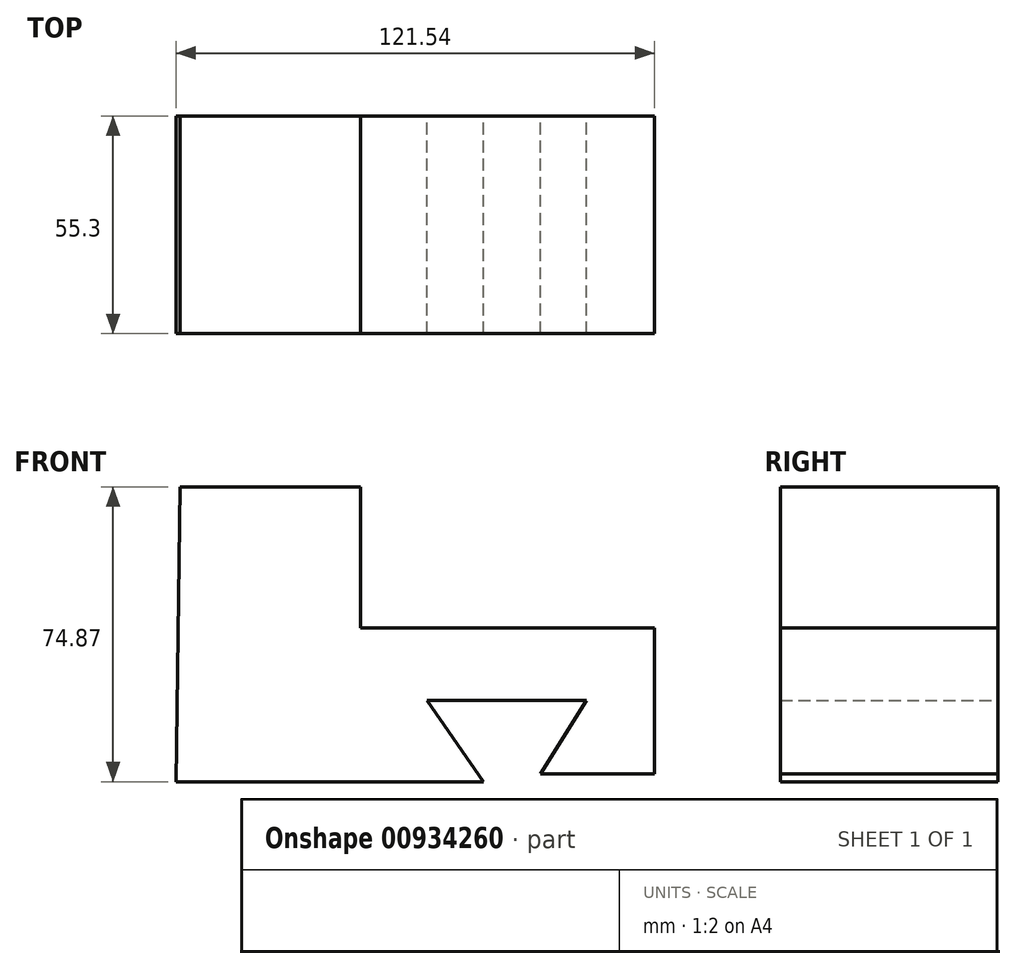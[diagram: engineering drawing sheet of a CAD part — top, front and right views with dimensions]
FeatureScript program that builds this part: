
annotation { "Feature Type Name" : "Feature", "Feature Type Description" : "" }
export const myFeature = defineFeature(function(context is Context, id is Id, definition is map)
    precondition{}
    {
        {
            var Q0;
            Q0=qCreatedBy(makeId("Front.planeOp"),FACE);
            var sketch = newSketch(context, id + "F0", { "sketchPlane" : qUnion([Q0])});
            skLineSegment(sketch, "E0", {"start": v(-78.14, -20.67) * mm, "end": v(0, -20.67) * mm});
            skLineSegment(sketch, "E1", {"start": v(0, -20.67) * mm, "end": v(0, -20.67) * mm});
            skLineSegment(sketch, "E2", {"start": v(0, -20.67) * mm, "end": v(-14.4, 0) * mm});
            skLineSegment(sketch, "E3", {"start": v(-14.4, 0) * mm, "end": v(26.07, 0) * mm});
            skLineSegment(sketch, "E4", {"start": v(26.07, 0) * mm, "end": v(14.5, -18.65) * mm});
            skLineSegment(sketch, "E5", {"start": v(14.5, -18.65) * mm, "end": v(43.4, -18.65) * mm});
            skLineSegment(sketch, "E6", {"start": v(43.4, -18.65) * mm, "end": v(43.4, 18.37) * mm});
            skLineSegment(sketch, "E7", {"start": v(43.4, 18.37) * mm, "end": v(-31.32, 18.37) * mm});
            skLineSegment(sketch, "E8", {"start": v(-31.32, 18.37) * mm, "end": v(-31.32, 54.2) * mm});
            skLineSegment(sketch, "E9", {"start": v(-31.32, 54.2) * mm, "end": v(-77.14, 54.2) * mm});
            skLineSegment(sketch, "E10", {"start": v(-78.14, -20.67) * mm, "end": v(-77.14, 54.2) * mm});
            skSolve(sketch);
        }
        {
            var Q0;
            Q0=makeQuery(id+"F0.imprint","IMPRINT",FACE,{"disambiguationData":[TD([[makeQuery(id+"F0.imprint","IMPRINT",EDGE,{"derivedFrom":sQuery(id+"F0.wireOp",EDGE,"E0")}),1.0]])]});
            extrude(context, id + "F1", {"entities" : qUnion([Q0]), "depth" : 55.3 * mm, "offsetDistance" : 25.4 * mm});
        }
    });
